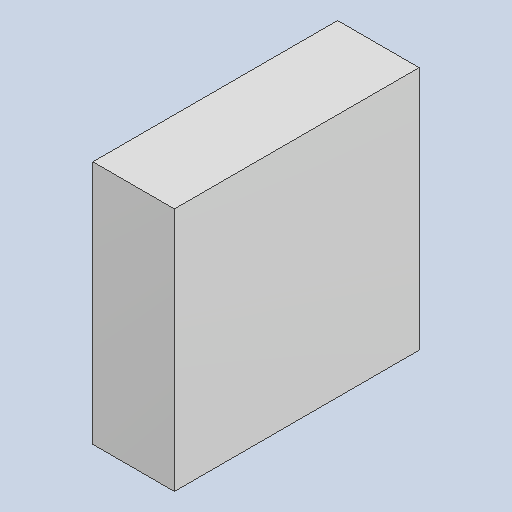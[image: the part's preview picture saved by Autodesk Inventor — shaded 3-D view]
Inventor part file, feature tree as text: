
AUTODESK INVENTOR PART (.ipt)
format: ipt  version: 2023.4 (Build 274418000, 418)  size: 81,408 bytes
history: native  units: mm
features: extrude x1
ambient origin geometry x8: Origin, YZ Plane, XZ Plane, XY Plane, X Axis, Y Axis, Z Axis, Center Point
bodies: Solid1 (feature_tree)
feature tree (1):
  extrude  "Extruded_36"  [1 undecoded]
note: 1 required parameter value undecoded (feature->parameter linkage not recoverable at this tier; creation-order binding heuristic only, values carry confidence <= 0.55)
